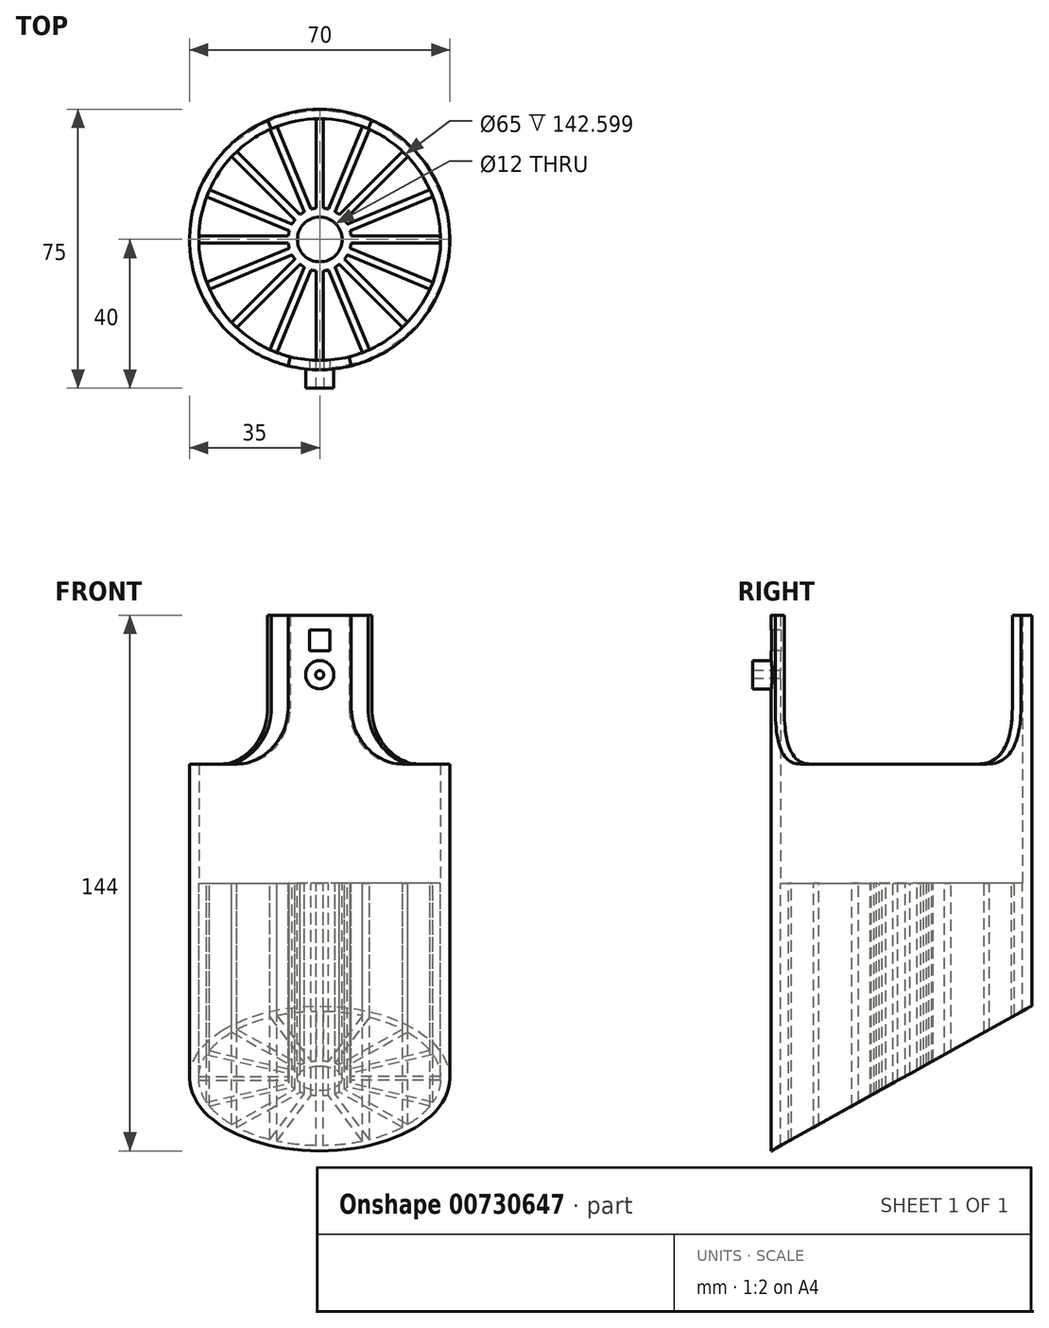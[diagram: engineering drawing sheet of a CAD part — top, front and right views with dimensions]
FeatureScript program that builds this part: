
annotation { "Feature Type Name" : "Feature", "Feature Type Description" : "" }
export const myFeature = defineFeature(function(context is Context, id is Id, definition is map)
    precondition{}
    {
        {
            var Q0;
            Q0=qCreatedBy(makeId("Top.planeOp"),FACE);
            var sketch = newSketch(context, id + "F0", { "sketchPlane" : qUnion([Q0])});
            skCircle(sketch, "E0", {"center": v(0, 0) * mm, "radius": 35 * mm});
            skCircle(sketch, "E1", {"center": v(0, 0) * mm, "radius": 6 * mm});
            skCircle(sketch, "E2.0", {"center": v(0, 0) * mm, "radius": 32.5 * mm});
            skCircle(sketch, "E3.0", {"center": v(0, 0) * mm, "radius": 8.5 * mm});
            skLineSegment(sketch, "E4", {"start": v(-1, 32.48) * mm, "end": v(-1, 8.44) * mm});
            skLineSegment(sketch, "E5", {"start": v(1, 32.48) * mm, "end": v(1, 8.44) * mm});
            skLineSegment(sketch, "E6.1.0", {"start": v(-13.36, 29.63) * mm, "end": v(-4.15, 7.42) * mm});
            skLineSegment(sketch, "E6.1.1", {"start": v(-11.5, 30.4) * mm, "end": v(-2.3, 8.18) * mm});
            skLineSegment(sketch, "E6.2.0", {"start": v(-23.68, 22.26) * mm, "end": v(-6.68, 5.26) * mm});
            skLineSegment(sketch, "E6.2.1", {"start": v(-22.26, 23.68) * mm, "end": v(-5.26, 6.68) * mm});
            skLineSegment(sketch, "E6.3.0", {"start": v(-30.4, 11.5) * mm, "end": v(-8.18, 2.3) * mm});
            skLineSegment(sketch, "E6.3.1", {"start": v(-29.63, 13.36) * mm, "end": v(-7.42, 4.15) * mm});
            skLineSegment(sketch, "E6.4.0", {"start": v(-32.48, -1) * mm, "end": v(-8.44, -1) * mm});
            skLineSegment(sketch, "E6.4.1", {"start": v(-32.48, 1) * mm, "end": v(-8.44, 1) * mm});
            skLineSegment(sketch, "E6.5.0", {"start": v(-29.63, -13.36) * mm, "end": v(-7.42, -4.15) * mm});
            skLineSegment(sketch, "E6.5.1", {"start": v(-30.4, -11.5) * mm, "end": v(-8.18, -2.3) * mm});
            skLineSegment(sketch, "E6.6.0", {"start": v(-22.26, -23.68) * mm, "end": v(-5.26, -6.68) * mm});
            skLineSegment(sketch, "E6.6.1", {"start": v(-23.68, -22.26) * mm, "end": v(-6.68, -5.26) * mm});
            skLineSegment(sketch, "E6.7.0", {"start": v(-11.5, -30.4) * mm, "end": v(-2.3, -8.18) * mm});
            skLineSegment(sketch, "E6.7.1", {"start": v(-13.36, -29.63) * mm, "end": v(-4.15, -7.42) * mm});
            skLineSegment(sketch, "E6.8.0", {"start": v(1, -32.48) * mm, "end": v(1, -8.44) * mm});
            skLineSegment(sketch, "E6.8.1", {"start": v(-1, -32.48) * mm, "end": v(-1, -8.44) * mm});
            skLineSegment(sketch, "E6.9.0", {"start": v(13.36, -29.63) * mm, "end": v(4.15, -7.42) * mm});
            skLineSegment(sketch, "E6.9.1", {"start": v(11.5, -30.4) * mm, "end": v(2.3, -8.18) * mm});
            skLineSegment(sketch, "E6.10.0", {"start": v(23.68, -22.26) * mm, "end": v(6.68, -5.26) * mm});
            skLineSegment(sketch, "E6.10.1", {"start": v(22.26, -23.68) * mm, "end": v(5.26, -6.68) * mm});
            skLineSegment(sketch, "E6.11.0", {"start": v(30.4, -11.5) * mm, "end": v(8.18, -2.3) * mm});
            skLineSegment(sketch, "E6.11.1", {"start": v(29.63, -13.36) * mm, "end": v(7.42, -4.15) * mm});
            skLineSegment(sketch, "E6.12.0", {"start": v(32.48, 1) * mm, "end": v(8.44, 1) * mm});
            skLineSegment(sketch, "E6.12.1", {"start": v(32.48, -1) * mm, "end": v(8.44, -1) * mm});
            skLineSegment(sketch, "E6.13.0", {"start": v(29.63, 13.36) * mm, "end": v(7.42, 4.15) * mm});
            skLineSegment(sketch, "E6.13.1", {"start": v(30.4, 11.5) * mm, "end": v(8.18, 2.3) * mm});
            skLineSegment(sketch, "E6.14.0", {"start": v(22.26, 23.68) * mm, "end": v(5.26, 6.68) * mm});
            skLineSegment(sketch, "E6.14.1", {"start": v(23.68, 22.26) * mm, "end": v(6.68, 5.26) * mm});
            skLineSegment(sketch, "E6.15.0", {"start": v(11.5, 30.4) * mm, "end": v(2.3, 8.18) * mm});
            skLineSegment(sketch, "E6.15.1", {"start": v(13.36, 29.63) * mm, "end": v(4.15, 7.42) * mm});
            skLineSegment(sketch, "E7", {"start": v(8.5, -33.95) * mm, "end": v(7.9, -31.53) * mm});
            skLineSegment(sketch, "E8", {"start": v(-8.5, -33.95) * mm, "end": v(-7.9, -31.53) * mm});
            skLineSegment(sketch, "E9", {"start": v(13, 29.79) * mm, "end": v(14, 32.08) * mm});
            skLineSegment(sketch, "E10", {"start": v(-13, 29.79) * mm, "end": v(-14, 32.08) * mm});
            skSolve(sketch);
        }
        {
            var Q0;
            Q0=makeQuery(id+"F0.imprint","IMPRINT",FACE,{"disambiguationData":[TD([[makeQuery(id+"F0.imprint","IMPRINT",EDGE,{"derivedFrom":sQuery(id+"F0.wireOp",EDGE,"E0")}),1.0]])]});
            var Q1;
            {var subQ4=sQuery(id+"F0.wireOp",EDGE,"E7");Q1=makeQuery(id+"F0.imprint","IMPRINT",FACE,{"disambiguationData":[TD([[makeQuery(id+"F0.imprint","IMPRINT",EDGE,{"derivedFrom":subQ4}),-1.0]])]});}
            var Q2;
            {var subQ3=sQuery(id+"F0.wireOp",EDGE,"E8");Q2=makeQuery(id+"F0.imprint","IMPRINT",FACE,{"disambiguationData":[TD([[makeQuery(id+"F0.imprint","IMPRINT",EDGE,{"derivedFrom":subQ3}),1.0]])]});}
            var Q3;
            {var subQ4=sQuery(id+"F0.wireOp",EDGE,"E9");Q3=makeQuery(id+"F0.imprint","IMPRINT",FACE,{"disambiguationData":[TD([[makeQuery(id+"F0.imprint","IMPRINT",EDGE,{"derivedFrom":subQ4}),1.0]])]});}
            extrude(context, id + "F1", {"entities" : qUnion([Q0, Q1, Q2, Q3]), "depth" : 32 * mm, "offsetDistance" : 25 * mm});
        }
        {
            var Q0;
            {var subQ4=sQuery(id+"F0.wireOp",EDGE,"E7");Q0=makeQuery(id+"F0.imprint","IMPRINT",FACE,{"disambiguationData":[TD([[makeQuery(id+"F0.imprint","IMPRINT",EDGE,{"derivedFrom":subQ4}),1.0]])]});}
            var Q1;
            {var subQ4=sQuery(id+"F0.wireOp",EDGE,"E9");Q1=makeQuery(id+"F0.imprint","IMPRINT",FACE,{"disambiguationData":[TD([[makeQuery(id+"F0.imprint","IMPRINT",EDGE,{"derivedFrom":subQ4}),1.0]])]});}
            extrude(context, id + "F2", {"entities" : qUnion([Q0, Q1]), "operationType" : NewBodyOperationType.ADD, "depth" : 72 * mm, "offsetDistance" : 25 * mm});
        }
        {
            var Q0;
            Q0=makeQuery(id+"F0.imprint","IMPRINT",FACE,{"disambiguationData":[TD([[makeQuery(id+"F0.imprint","IMPRINT",EDGE,{"derivedFrom":sQuery(id+"F0.wireOp",EDGE,"E0")}),1.0]])]});
            var Q1;
            {var subQ0=sQuery(id+"F0.wireOp",EDGE,"E6.14.0");Q1=makeQuery(id+"F0.imprint","IMPRINT",FACE,{"disambiguationData":[TD([[makeQuery(id+"F0.imprint","IMPRINT",EDGE,{"derivedFrom":subQ0}),1.0]])]});}
            var Q2;
            {var subQ0=sQuery(id+"F0.wireOp",EDGE,"E6.1.0");Q2=makeQuery(id+"F0.imprint","IMPRINT",FACE,{"disambiguationData":[TD([[makeQuery(id+"F0.imprint","IMPRINT",EDGE,{"derivedFrom":subQ0}),1.0]])]});}
            var Q3;
            {var subQ0=sQuery(id+"F0.wireOp",EDGE,"E6.15.0");Q3=makeQuery(id+"F0.imprint","IMPRINT",FACE,{"disambiguationData":[TD([[makeQuery(id+"F0.imprint","IMPRINT",EDGE,{"derivedFrom":subQ0}),1.0]])]});}
            var Q4;
            {var subQ0=sQuery(id+"F0.wireOp",EDGE,"E6.13.0");Q4=makeQuery(id+"F0.imprint","IMPRINT",FACE,{"disambiguationData":[TD([[makeQuery(id+"F0.imprint","IMPRINT",EDGE,{"derivedFrom":subQ0}),1.0]])]});}
            var Q5;
            {var subQ0=sQuery(id+"F0.wireOp",EDGE,"E6.12.0");Q5=makeQuery(id+"F0.imprint","IMPRINT",FACE,{"disambiguationData":[TD([[makeQuery(id+"F0.imprint","IMPRINT",EDGE,{"derivedFrom":subQ0}),1.0]])]});}
            var Q6;
            {var subQ0=sQuery(id+"F0.wireOp",EDGE,"E6.11.0");Q6=makeQuery(id+"F0.imprint","IMPRINT",FACE,{"disambiguationData":[TD([[makeQuery(id+"F0.imprint","IMPRINT",EDGE,{"derivedFrom":subQ0}),1.0]])]});}
            var Q7;
            {var subQ0=sQuery(id+"F0.wireOp",EDGE,"E6.10.0");Q7=makeQuery(id+"F0.imprint","IMPRINT",FACE,{"disambiguationData":[TD([[makeQuery(id+"F0.imprint","IMPRINT",EDGE,{"derivedFrom":subQ0}),1.0]])]});}
            var Q8;
            {var subQ0=sQuery(id+"F0.wireOp",EDGE,"E6.9.0");Q8=makeQuery(id+"F0.imprint","IMPRINT",FACE,{"disambiguationData":[TD([[makeQuery(id+"F0.imprint","IMPRINT",EDGE,{"derivedFrom":subQ0}),1.0]])]});}
            var Q9;
            {var subQ0=sQuery(id+"F0.wireOp",EDGE,"E6.8.0");Q9=makeQuery(id+"F0.imprint","IMPRINT",FACE,{"disambiguationData":[TD([[makeQuery(id+"F0.imprint","IMPRINT",EDGE,{"derivedFrom":subQ0}),1.0]])]});}
            var Q10;
            {var subQ0=sQuery(id+"F0.wireOp",EDGE,"E6.7.0");Q10=makeQuery(id+"F0.imprint","IMPRINT",FACE,{"disambiguationData":[TD([[makeQuery(id+"F0.imprint","IMPRINT",EDGE,{"derivedFrom":subQ0}),1.0]])]});}
            var Q11;
            {var subQ0=sQuery(id+"F0.wireOp",EDGE,"E6.6.0");Q11=makeQuery(id+"F0.imprint","IMPRINT",FACE,{"disambiguationData":[TD([[makeQuery(id+"F0.imprint","IMPRINT",EDGE,{"derivedFrom":subQ0}),1.0]])]});}
            var Q12;
            {var subQ0=sQuery(id+"F0.wireOp",EDGE,"E6.5.0");Q12=makeQuery(id+"F0.imprint","IMPRINT",FACE,{"disambiguationData":[TD([[makeQuery(id+"F0.imprint","IMPRINT",EDGE,{"derivedFrom":subQ0}),1.0]])]});}
            var Q13;
            {var subQ0=sQuery(id+"F0.wireOp",EDGE,"E6.4.0");Q13=makeQuery(id+"F0.imprint","IMPRINT",FACE,{"disambiguationData":[TD([[makeQuery(id+"F0.imprint","IMPRINT",EDGE,{"derivedFrom":subQ0}),1.0]])]});}
            var Q14;
            {var subQ0=sQuery(id+"F0.wireOp",EDGE,"E6.3.0");Q14=makeQuery(id+"F0.imprint","IMPRINT",FACE,{"disambiguationData":[TD([[makeQuery(id+"F0.imprint","IMPRINT",EDGE,{"derivedFrom":subQ0}),1.0]])]});}
            var Q15;
            {var subQ0=sQuery(id+"F0.wireOp",EDGE,"E6.2.0");Q15=makeQuery(id+"F0.imprint","IMPRINT",FACE,{"disambiguationData":[TD([[makeQuery(id+"F0.imprint","IMPRINT",EDGE,{"derivedFrom":subQ0}),1.0]])]});}
            var Q16;
            Q16=makeQuery(id+"F0.imprint","IMPRINT",FACE,{"disambiguationData":[TD([[makeQuery(id+"F0.imprint","IMPRINT",EDGE,{"derivedFrom":sQuery(id+"F0.wireOp",EDGE,"E1")}),-1.0]])]});
            var Q17;
            {var subQ0=sQuery(id+"F0.wireOp",EDGE,"E4");Q17=makeQuery(id+"F0.imprint","IMPRINT",FACE,{"disambiguationData":[TD([[makeQuery(id+"F0.imprint","IMPRINT",EDGE,{"derivedFrom":subQ0}),1.0]])]});}
            var Q18;
            {var subQ3=sQuery(id+"F0.wireOp",EDGE,"E8");Q18=makeQuery(id+"F0.imprint","IMPRINT",FACE,{"disambiguationData":[TD([[makeQuery(id+"F0.imprint","IMPRINT",EDGE,{"derivedFrom":subQ3}),1.0]])]});}
            var Q19;
            {var subQ4=sQuery(id+"F0.wireOp",EDGE,"E9");Q19=makeQuery(id+"F0.imprint","IMPRINT",FACE,{"disambiguationData":[TD([[makeQuery(id+"F0.imprint","IMPRINT",EDGE,{"derivedFrom":subQ4}),1.0]])]});}
            var Q20;
            {var subQ4=sQuery(id+"F0.wireOp",EDGE,"E7");Q20=makeQuery(id+"F0.imprint","IMPRINT",FACE,{"disambiguationData":[TD([[makeQuery(id+"F0.imprint","IMPRINT",EDGE,{"derivedFrom":subQ4}),-1.0]])]});}
            extrude(context, id + "F3", {"entities" : qUnion([Q0, Q1, Q2, Q3, Q4, Q5, Q6, Q7, Q8, Q9, Q10, Q11, Q12, Q13, Q14, Q15, Q16, Q17, Q18, Q19, Q20]), "operationType" : NewBodyOperationType.ADD, "oppositeDirection" : true, "depth" : 72 * mm, "offsetDistance" : 25 * mm});
        }
        {
            var Q0;
            Q0=qCreatedBy(makeId("Right.planeOp"),FACE);
            var sketch = newSketch(context, id + "F4", { "sketchPlane" : qUnion([Q0])});
            skLineSegment(sketch, "E11", {"start": v(35, 67) * mm, "end": v(35, -72) * mm, "construction": true});
            skLineSegment(sketch, "E12.0", {"start": v(-35, -72) * mm, "end": v(35, -72) * mm, "construction": true});
            skLineSegment(sketch, "E13", {"start": v(-35, -72) * mm, "end": v(35, -33) * mm});
            skLineSegment(sketch, "E14", {"start": v(35, -33) * mm, "end": v(35, -72) * mm});
            skLineSegment(sketch, "E15", {"start": v(-35, -72) * mm, "end": v(35, -72) * mm});
            skSolve(sketch);
        }
        {
            var Q0;
            Q0=qSketchRegion(id+"F4",true);
            extrude(context, id + "F5", {"entities" : qUnion([Q0]), "operationType" : NewBodyOperationType.REMOVE, "oppositeDirection" : true, "depth" : 80 * mm, "offsetDistance" : 25 * mm, "symmetric" : true});
        }
        {
            var Q0;
            Q0=qCreatedBy(makeId("Front.planeOp"),FACE);
            cPlane(context, id + "F6", {"entities" : qUnion([Q0]), "cplaneType" : CPlaneType.OFFSET, "offset" : 40 * mm, "width" : 150 * mm, "height" : 150 * mm});
        }
        {
            var Q0;
            Q0=qCreatedBy(id+"F6.planeOp",FACE);
            var sketch = newSketch(context, id + "F7", { "sketchPlane" : qUnion([Q0])});
            skLineSegment(sketch, "E16.bottom", {"start": v(2.75, 68) * mm, "end": v(-2.75, 68) * mm});
            skLineSegment(sketch, "E16.top", {"start": v(2.75, 62.5) * mm, "end": v(-2.75, 62.5) * mm});
            skLineSegment(sketch, "E16.left", {"start": v(2.75, 68) * mm, "end": v(2.75, 62.5) * mm});
            skLineSegment(sketch, "E16.right", {"start": v(-2.75, 68) * mm, "end": v(-2.75, 62.5) * mm});
            skCircle(sketch, "E17", {"center": v(0, 56) * mm, "radius": 3.8 * mm});
            skCircle(sketch, "E18", {"center": v(0, 56) * mm, "radius": 1.1 * mm});
            skLineSegment(sketch, "E19.0", {"start": v(-8.5, 72) * mm, "end": v(8.5, 72) * mm, "construction": true});
            skSolve(sketch);
        }
        {
            var Q0;
            Q0=makeQuery(id+"F7.imprint","IMPRINT",FACE,{"disambiguationData":[TD([[makeQuery(id+"F7.imprint","IMPRINT",EDGE,{"derivedFrom":sQuery(id+"F7.wireOp",EDGE,"E17")}),1.0]])]});
            extrude(context, id + "F8", {"entities" : qUnion([Q0]), "operationType" : NewBodyOperationType.ADD, "oppositeDirection" : true, "depth" : 5.4 * mm, "offsetDistance" : 25 * mm});
        }
        {
            var Q0;
            Q0=makeQuery(id+"F7.imprint","IMPRINT",FACE,{"disambiguationData":[TD([[makeQuery(id+"F7.imprint","IMPRINT",EDGE,{"derivedFrom":sQuery(id+"F7.wireOp",EDGE,"E16.bottom")}),1.0]])]});
            var Q1;
            Q1=makeQuery(id+"F7.imprint","IMPRINT",FACE,{"disambiguationData":[TD([[makeQuery(id+"F7.imprint","IMPRINT",EDGE,{"derivedFrom":sQuery(id+"F7.wireOp",EDGE,"E18")}),1.0]])]});
            extrude(context, id + "F9", {"entities" : qUnion([Q0, Q1]), "operationType" : NewBodyOperationType.REMOVE, "oppositeDirection" : true, "depth" : 25 * mm, "offsetDistance" : 25 * mm});
        }
        {
            var Q0;
            Q0=makeQuery(id+"F2.boolean.opBoolean","INTERSECT",EDGE,{"derivedFrom":[makeQuery(id+"F1.opExtrude","CAP_FACE",FACE,{"disambiguationData":[OSD([sQuery(id+"F0.wireOp",EDGE,"E0"),sQuery(id+"F0.wireOp",EDGE,"E2.0")])],"isStart":false}),makeQuery(id+"F2.opExtrude","SWEPT_FACE",FACE,{"disambiguationData":[OSD([sQuery(id+"F0.wireOp",EDGE,"E8")])]})]});
            var Q1;
            Q1=makeQuery(id+"F2.boolean.opBoolean","INTERSECT",EDGE,{"derivedFrom":[makeQuery(id+"F1.opExtrude","CAP_FACE",FACE,{"disambiguationData":[OSD([sQuery(id+"F0.wireOp",EDGE,"E0"),sQuery(id+"F0.wireOp",EDGE,"E2.0")])],"isStart":false}),makeQuery(id+"F2.opExtrude","SWEPT_FACE",FACE,{"disambiguationData":[OSD([sQuery(id+"F0.wireOp",EDGE,"E7")])]})]});
            var Q2;
            Q2=makeQuery(id+"F2.boolean.opBoolean","INTERSECT",EDGE,{"derivedFrom":[makeQuery(id+"F1.opExtrude","CAP_FACE",FACE,{"disambiguationData":[OSD([sQuery(id+"F0.wireOp",EDGE,"E0"),sQuery(id+"F0.wireOp",EDGE,"E2.0")])],"isStart":false}),makeQuery(id+"F2.opExtrude","SWEPT_FACE",FACE,{"disambiguationData":[OSD([sQuery(id+"F0.wireOp",EDGE,"E10")])]})]});
            var Q3;
            Q3=makeQuery(id+"F2.boolean.opBoolean","INTERSECT",EDGE,{"derivedFrom":[makeQuery(id+"F1.opExtrude","CAP_FACE",FACE,{"disambiguationData":[OSD([sQuery(id+"F0.wireOp",EDGE,"E0"),sQuery(id+"F0.wireOp",EDGE,"E2.0")])],"isStart":false}),makeQuery(id+"F2.opExtrude","SWEPT_FACE",FACE,{"disambiguationData":[OSD([sQuery(id+"F0.wireOp",EDGE,"E9")])]})]});
            fillet(context, id + "F10", {"entities" : qUnion([Q0, Q1, Q2, Q3]), "radius" : 15 * mm, "tangentPropagation" : true, "allowEdgeOverflow" : false});
        }
    });
